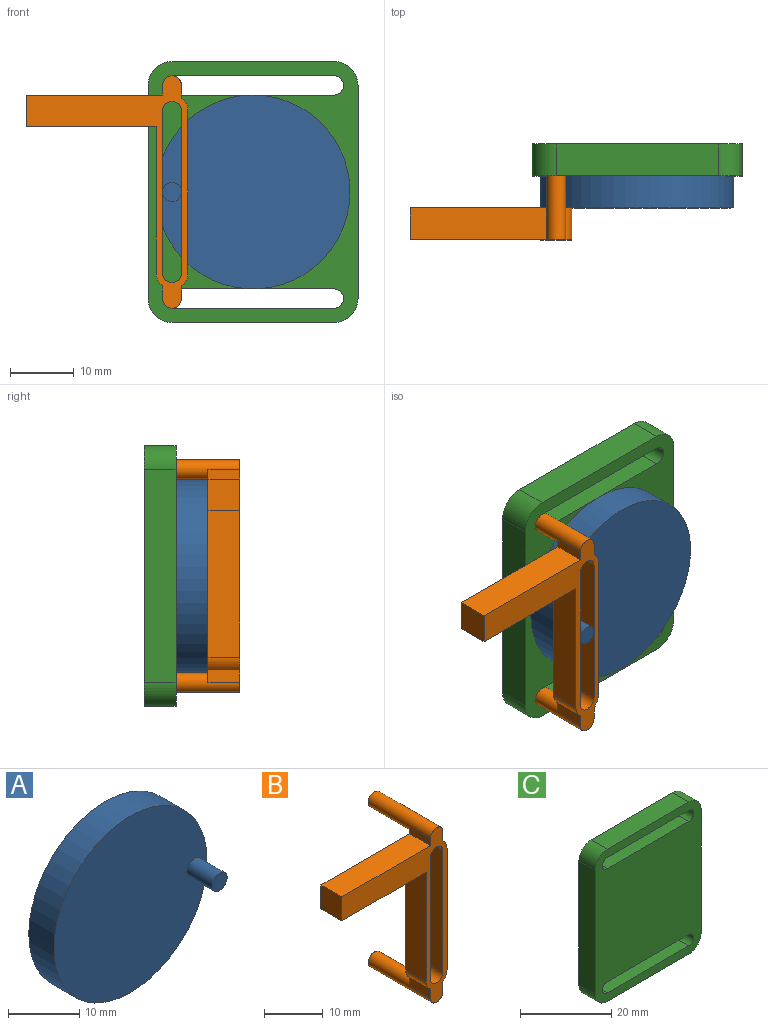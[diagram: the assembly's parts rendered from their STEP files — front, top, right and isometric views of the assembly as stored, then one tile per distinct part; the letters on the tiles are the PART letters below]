
ASSEMBLY  parts=3 mates=4
PART A: 5 faces, bbox 30.4x10x30.4 mm
  f0: cylinder r=15.2mm len=30.4mm, axis (0,1,0), area 477.5mm2, adj f1,f2
  f1: plane 30.4x30.4mm, normal (0,-1,0), area 718.8mm2, adj f0,f3
  f2: plane 30.4x30.4mm, normal (0,1,0), area 725.8mm2, adj f0
  f3: cylinder r=1.5mm len=5mm, axis (0,1,0), area 47.1mm2, adj f1,f4
  f4: plane 3x3mm, normal (0,-1,0), area 7.1mm2, adj f3
PART B: 22 faces, bbox 25.4x15x36.4 mm
  f0: plane 20.39x5mm, normal (0,0,-1), area 102mm2, adj f1,f15,f16,f17
  f1: plane 22.9x5mm, normal (-1,0,0), area 114.5mm2, adj f0,f2,f16,f17
  f2: cylinder r=2.5mm len=5mm, axis (0,1,0), area 11.6mm2, adj f1,f3,f16,f17
  f3: plane 5x2mm, normal (-1,0,0), area 10mm2, adj f2,f16,f17,f20
  f4: plane 5x2mm, normal (1,0,0), area 10mm2, adj f5,f16,f17,f20
  f5: cylinder r=2.5mm len=5mm, axis (0,1,0), area 11.6mm2, adj f4,f6,f16,f17
  f6: plane 25.4x5mm, normal (1,0,0), area 127mm2, adj f5,f7,f16,f17
  f7: cylinder r=2.5mm len=5mm, axis (0,1,0), area 11.6mm2, adj f6,f8,f16,f17
  f8: plane 5x2mm, normal (1,0,0), area 10mm2, adj f7,f16,f17,f18
  f9: plane 5x1.5mm, normal (-1,0,0), area 7.5mm2, adj f10,f16,f17,f18
  f10: plane 21.39x5mm, normal (0,0,1), area 107mm2, adj f9,f15,f16,f17
  f11: plane 25.4x5mm, normal (1,0,0), area 127mm2, adj f12,f14,f16,f17
  f12: cylinder r=1.5mm len=5mm, axis (0,1,0), area 23.6mm2, adj f11,f13,f16,f17
  f13: plane 25.4x5mm, normal (-1,0,0), area 127mm2, adj f12,f14,f16,f17
  f14: cylinder r=1.5mm len=5mm, axis (0,1,0), area 23.6mm2, adj f11,f13,f16,f17
  f15: plane 5x5mm, normal (-1,0,0), area 25mm2, adj f0,f10,f16,f17
  f16: plane 36.4x25.39mm, normal (0,-1,0), area 183.4mm2, adj f0,f1,f2,f3,f4,f5,f6,f7
  f17: plane 33.4x25.39mm, normal (0,1,0), area 169.3mm2, adj f0,f1,f2,f3,f4,f5,f6,f7
  f18: cylinder r=1.5mm len=15mm, axis (0,1,0), area 117.8mm2, adj f8,f9,f16,f17,f19
  f19: plane 3x3mm, normal (0,1,0), area 7.1mm2, adj f18
  f20: cylinder r=1.5mm len=15mm, axis (0,1,0), area 117.8mm2, adj f3,f4,f16,f17,f21
  f21: plane 3x3mm, normal (0,1,0), area 7.1mm2, adj f20
PART C: 18 faces, bbox 32.9x5x40.9 mm
  f0: cylinder r=1.5mm len=5mm, axis (0,1,0), area 23.6mm2, adj f1,f15,f16,f17
  f1: plane 25.4x5mm, normal (0,0,-1), area 127mm2, adj f0,f2,f16,f17
  f2: cylinder r=1.5mm len=5mm, axis (0,1,0), area 23.6mm2, adj f1,f15,f16,f17
  f3: plane 25.4x5mm, normal (0,0,1), area 127mm2, adj f4,f13,f16,f17
  f4: cylinder r=1.5mm len=5mm, axis (0,1,0), area 23.6mm2, adj f3,f5,f16,f17
  f5: plane 25.4x5mm, normal (0,0,-1), area 127mm2, adj f4,f13,f16,f17
  f6: plane 33.4x5mm, normal (-1,0,0), area 167mm2, adj f7,f14,f16,f17
  f7: cylinder r=3.75mm len=5mm, axis (0,1,0), area 29.5mm2, adj f6,f8,f16,f17
  f8: plane 25.4x5mm, normal (0,0,-1), area 127mm2, adj f7,f9,f16,f17
  f9: cylinder r=3.75mm len=5mm, axis (0,1,0), area 29.5mm2, adj f8,f10,f16,f17
  f10: plane 33.4x5mm, normal (1,0,0), area 167mm2, adj f9,f11,f16,f17
  f11: cylinder r=3.75mm len=5mm, axis (0,1,0), area 29.5mm2, adj f10,f12,f16,f17
  f12: plane 25.4x5mm, normal (0,0,1), area 127mm2, adj f11,f14,f16,f17
  f13: cylinder r=1.5mm len=5mm, axis (0,1,0), area 23.6mm2, adj f3,f5,f16,f17
  f14: cylinder r=3.75mm len=5mm, axis (0,1,0), area 29.5mm2, adj f6,f12,f16,f17
  f15: plane 25.4x5mm, normal (0,0,1), area 127mm2, adj f0,f2,f16,f17
  f16: plane 40.9x32.9mm, normal (0,-1,0), area 1167mm2, adj f0,f1,f2,f3,f4,f5,f6,f7
  f17: plane 40.9x32.9mm, normal (0,1,0), area 1167mm2, adj f0,f1,f2,f3,f4,f5,f6,f7
PLACE A rot(axis=(0,-1,0),180deg) t=(0,0,0)mm
PLACE B t=(-12.7,-5,0)mm
PLACE C rot(axis=(0,-1,0),0deg) t=(12.7,5,-0.25)mm
MATE pin_slot B.f12 <-> A.f3  axis (0,-1,0) through (-12.7,-10,12.7)mm
MATE pin_slot B.f18 <-> C.f4  axis (0,1,0) through (-12.7,5,16.7)mm
MATE planar C.f16 <-> A.f0  axis (0,-1,0) through (0,0,0)mm
MATE pin_slot C.f0 <-> B.f20  axis (0,1,0) through (-12.7,5,-16.7)mm
